# Revit family: Reece_Toilet_Base_Link_S Trap
name_source: partatom
category: Plumbing Fixtures
revit_build: Autodesk Revit 2018 (Build: 20190510_1515(x64)
units: mm (PartAtom-declared; Revit-internal decimal feet)

## family parameters
Always vertical = Yes
Cut with Voids When Loaded = No
Part Type = Normal
Room Calculation Point = No
Round Connector Dimension = Use Diameter
Shared = No
Work Plane-Based = No

## types (1)
- Standard_Bottom Inlet_White
    Description = BASE Link Toilet Suite S Trap with Seat White (4 Star)
    Disclaimer = THIS FILE IS THE PROPERTY OF THE REECE GROUP. IT MAY NOT BE REPRODUCED, REVERSE-ENGINEERED OR MODIFIED. ANY REPUBLICATION, TRANSMISSION OR DISTRIBUTION FOR THE PURPOSE OF COMMERCIALLY EXPLOITING THE FILES IS PROHIBITED.
    Keynote = Product #9503292, Reece_Toilet_Base_Link_S Trap - Standard_Bottom Inlet_White
    Manufacturer = Base
    Model = Base
    Reece_Bottom_Outlet_Offset = 165 mm
    Reece_Detail_Additional = Link
    Reece_Detail_Connector = Bottom Inlet (Reversible right or left)
    Reece_Detail_Disclaimer = THIS FILE IS THE PROPERTY OF THE REECE GROUP. IT MAY NOT BE REPRODUCED, REVERSE-ENGINEERED OR MODIFIED. ANY REPUBLICATION, TRANSMISSION OR DISTRIBUTION FOR THE PURPOSE OF COMMERCIALLY EXPLOITING THE FILES IS PROHIBITED.
    Reece_Detail_Function = S Trap
    Reece_Material_Cistern = Reece_Plastic_Urea_White
    Reece_Material_Main = Reece_Vitreous China_White
    Reece_Material_Seat = Reece_Plastic_Urea_White
    Reece_Overall_Height = 850 mm  [stored 2.78871 ft]
    Reece_Overall_Projection = 650 mm  [stored 2.13255 ft]
    Reece_Overall_Width = 418 mm  [stored 1.37139 ft]
    Reece_P_Trap = 102 mm
    Reece_Product_Brand = Base
    Reece_Product_Description = BASE Link Toilet Suite S Trap with Seat White (4 Star)
    Reece_Product_Mount = Floor Mounted
    Reece_Product_Number = 9503292
    Reece_Product_Sub Brand = Base
    Reece_Product_Type = Toilet
    Reece_Product_Web Page = https://www.reece.com.au
    Reece_S_Trap = 102 mm
    Reece_Seat_Height = 395 mm  [stored 1.29593 ft]
    Type Comments = Toilet
    URL = https://www.reece.com.au

note: [stored X ft] marks values corroborated as IEEE doubles in the binary element streams (Revit-internal decimal feet)

## geometry (parser evidence)
native form markers: Sweep x10
no freeform markers — native parametric forms only
